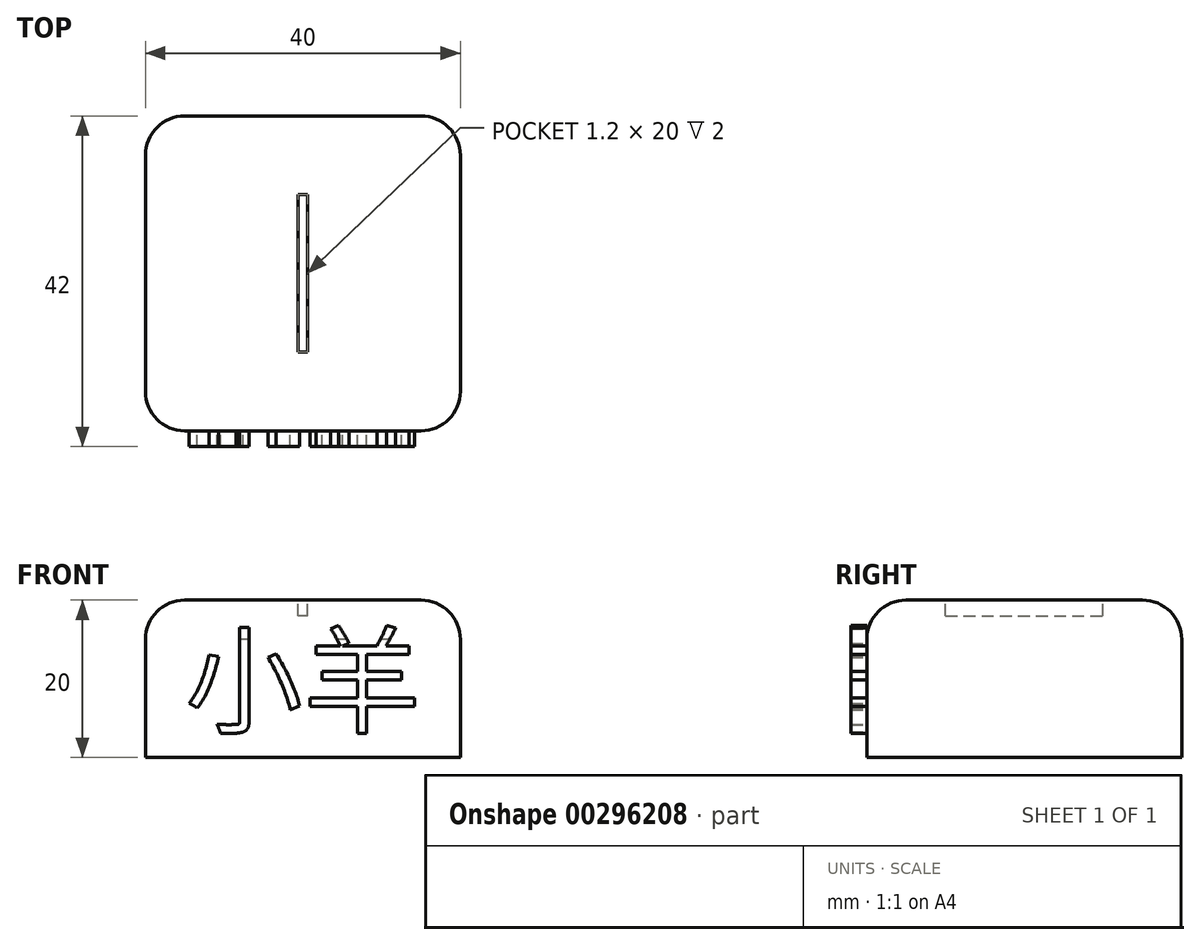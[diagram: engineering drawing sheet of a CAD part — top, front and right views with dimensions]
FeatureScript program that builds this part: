
annotation { "Feature Type Name" : "Feature", "Feature Type Description" : "" }
export const myFeature = defineFeature(function(context is Context, id is Id, definition is map)
    precondition{}
    {
        {
            var Q0;
            Q0=qCreatedBy(makeId("Top.planeOp"),FACE);
            var sketch = newSketch(context, id + "F0", { "sketchPlane" : qUnion([Q0])});
            skLineSegment(sketch, "E0.bottom", {"start": v(20, -20) * mm, "end": v(-20, -20) * mm});
            skLineSegment(sketch, "E0.top", {"start": v(20, 20) * mm, "end": v(-20, 20) * mm});
            skLineSegment(sketch, "E0.left", {"start": v(20, -20) * mm, "end": v(20, 20) * mm});
            skLineSegment(sketch, "E0.right", {"start": v(-20, -20) * mm, "end": v(-20, 20) * mm});
            skPoint(sketch, "E0.middle", {"position": v(0, 0) * mm});
            skLineSegment(sketch, "E1.bottom", {"start": v(0.6, -10) * mm, "end": v(-0.6, -10) * mm});
            skLineSegment(sketch, "E1.top", {"start": v(0.6, 10) * mm, "end": v(-0.6, 10) * mm});
            skLineSegment(sketch, "E1.left", {"start": v(0.6, -10) * mm, "end": v(0.6, 10) * mm});
            skLineSegment(sketch, "E1.right", {"start": v(-0.6, -10) * mm, "end": v(-0.6, 10) * mm});
            skSolve(sketch);
        }
        {
            var Q0;
            Q0=makeQuery(id+"F0.imprint","IMPRINT",FACE,{"disambiguationData":[TD([[makeQuery(id+"F0.imprint","IMPRINT",EDGE,{"derivedFrom":sQuery(id+"F0.wireOp",EDGE,"E0.bottom")}),-1.0]])]});
            var Q1;
            Q1=makeQuery(id+"F0.imprint","IMPRINT",FACE,{"disambiguationData":[TD([[makeQuery(id+"F0.imprint","IMPRINT",EDGE,{"derivedFrom":sQuery(id+"F0.wireOp",EDGE,"E1.bottom")}),-1.0]])]});
            extrude(context, id + "F1", {"entities" : qUnion([Q0, Q1]), "oppositeDirection" : true, "depth" : 20 * mm});
        }
        {
            var Q0;
            Q0=makeQuery(id+"F0.imprint","IMPRINT",FACE,{"disambiguationData":[TD([[makeQuery(id+"F0.imprint","IMPRINT",EDGE,{"derivedFrom":sQuery(id+"F0.wireOp",EDGE,"E1.bottom")}),-1.0]])]});
            extrude(context, id + "F2", {"entities" : qUnion([Q0]), "operationType" : NewBodyOperationType.REMOVE, "oppositeDirection" : true, "depth" : 2 * mm});
        }
        {
            var Q0;
            Q0=makeQuery(id+"F2.boolean.opBoolean","COPY",EDGE,{"derivedFrom":makeQuery(id+"F2.opExtrude","CAP_EDGE",EDGE,{"disambiguationData":[OSD([sQuery(id+"F0.wireOp",EDGE,"E1.left")])],"isStart":true})});
            var Q1;
            Q1=makeQuery(id+"F2.boolean.opBoolean","COPY",EDGE,{"derivedFrom":makeQuery(id+"F2.opExtrude","CAP_EDGE",EDGE,{"disambiguationData":[OSD([sQuery(id+"F0.wireOp",EDGE,"E1.right")])],"isStart":true})});
            var Q2;
            Q2=makeQuery(id+"F1.opExtrude","SWEPT_EDGE",EDGE,{"disambiguationData":[OSD([sQuery(id+"F0.wireOp",EDGE,"E0.bottom"),sQuery(id+"F0.wireOp",EDGE,"E0.left")])]});
            var Q3;
            Q3=makeQuery(id+"F1.opExtrude","SWEPT_EDGE",EDGE,{"disambiguationData":[OSD([sQuery(id+"F0.wireOp",EDGE,"E0.top"),sQuery(id+"F0.wireOp",EDGE,"E0.left")])]});
            var Q4;
            Q4=makeQuery(id+"F1.opExtrude","CAP_EDGE",EDGE,{"disambiguationData":[OSD([sQuery(id+"F0.wireOp",EDGE,"E0.left")])],"isStart":true});
            var Q5;
            Q5=makeQuery(id+"F1.opExtrude","SWEPT_EDGE",EDGE,{"disambiguationData":[OSD([sQuery(id+"F0.wireOp",EDGE,"E0.bottom"),sQuery(id+"F0.wireOp",EDGE,"E0.right")])]});
            var Q6;
            Q6=makeQuery(id+"F1.opExtrude","SWEPT_EDGE",EDGE,{"disambiguationData":[OSD([sQuery(id+"F0.wireOp",EDGE,"E0.top"),sQuery(id+"F0.wireOp",EDGE,"E0.right")])]});
            var Q7;
            Q7=makeQuery(id+"F1.opExtrude","CAP_EDGE",EDGE,{"disambiguationData":[OSD([sQuery(id+"F0.wireOp",EDGE,"E0.top")])],"isStart":true});
            var Q8;
            Q8=makeQuery(id+"F1.opExtrude","CAP_EDGE",EDGE,{"disambiguationData":[OSD([sQuery(id+"F0.wireOp",EDGE,"E0.right")])],"isStart":true});
            var Q9;
            Q9=makeQuery(id+"F1.opExtrude","CAP_EDGE",EDGE,{"disambiguationData":[OSD([sQuery(id+"F0.wireOp",EDGE,"E0.bottom")])],"isStart":true});
            fillet(context, id + "F3", {"entities" : qUnion([Q0, Q1, Q2, Q3, Q4, Q5, Q6, Q7, Q8, Q9]), "radius" : 5 * mm, "tangentPropagation" : true, "allowEdgeOverflow" : false});
        }
        {
            var Q0;
            Q0=makeQuery(id+"F1.opExtrude","SWEPT_FACE",FACE,{"disambiguationData":[OSD([sQuery(id+"F0.wireOp",EDGE,"E0.bottom")])]});
            var sketch = newSketch(context, id + "F4", { "sketchPlane" : qUnion([Q0])});
            skText(sketch, "E2", { "text": "小羊", "fontName": "NotoSansCJKtc-Regular.otf"});
            const initialGuessF4  = {"E2": [-0.015, -0.01581, 1, 0, 0.01081]};
            skSetInitialGuess(sketch, initialGuessF4);
            skSolve(sketch);
        }
        {
            var Q0;
            {var subQ0=sQuery(id+"F4.wireOp",EDGE,"E2.sketch_text.stroke-26");Q0=makeQuery(id+"F4.imprint","IMPRINT",FACE,{"disambiguationData":[TD([[makeQuery(id+"F4.imprint","IMPRINT",EDGE,{"derivedFrom":subQ0}),1.0]])]});}
            var Q1;
            {var subQ0=sQuery(id+"F4.wireOp",EDGE,"E2.sketch_text.stroke-31");Q1=makeQuery(id+"F4.imprint","IMPRINT",FACE,{"disambiguationData":[TD([[makeQuery(id+"F4.imprint","IMPRINT",EDGE,{"derivedFrom":subQ0}),1.0]])]});}
            var Q2;
            Q2=makeQuery(id+"F4.imprint","IMPRINT",FACE,{"disambiguationData":[TD([[makeQuery(id+"F4.imprint","IMPRINT",EDGE,{"derivedFrom":sQuery(id+"F4.wireOp",EDGE,"E2.sketch_text.stroke-16")}),1.0]])]});
            var Q3;
            {var subQ0=sQuery(id+"F4.wireOp",EDGE,"E2.sketch_text.stroke-1");Q3=makeQuery(id+"F4.imprint","IMPRINT",FACE,{"disambiguationData":[TD([[makeQuery(id+"F4.imprint","IMPRINT",EDGE,{"derivedFrom":subQ0}),1.0]])]});}
            var Q4;
            {var subQ0=sQuery(id+"F4.wireOp",EDGE,"E2.sketch_text.stroke-7");Q4=makeQuery(id+"F4.imprint","IMPRINT",FACE,{"disambiguationData":[TD([[makeQuery(id+"F4.imprint","IMPRINT",EDGE,{"derivedFrom":subQ0}),1.0]])]});}
            var Q5;
            Q5=makeQuery(id+"F4.imprint","IMPRINT",FACE,{"disambiguationData":[TD([[makeQuery(id+"F4.imprint","IMPRINT",EDGE,{"derivedFrom":sQuery(id+"F4.wireOp",EDGE,"E2.sketch_text.stroke-8")}),1.0]])]});
            var Q6;
            Q6=makeQuery(id+"F4.imprint","IMPRINT",FACE,{"disambiguationData":[TD([[makeQuery(id+"F4.imprint","IMPRINT",EDGE,{"derivedFrom":sQuery(id+"F4.wireOp",EDGE,"E2.sketch_text.stroke-12")}),1.0]])]});
            extrude(context, id + "F5", {"entities" : qUnion([Q0, Q1, Q2, Q3, Q4, Q5, Q6]), "operationType" : NewBodyOperationType.ADD, "depth" : 2 * mm});
        }
    });
